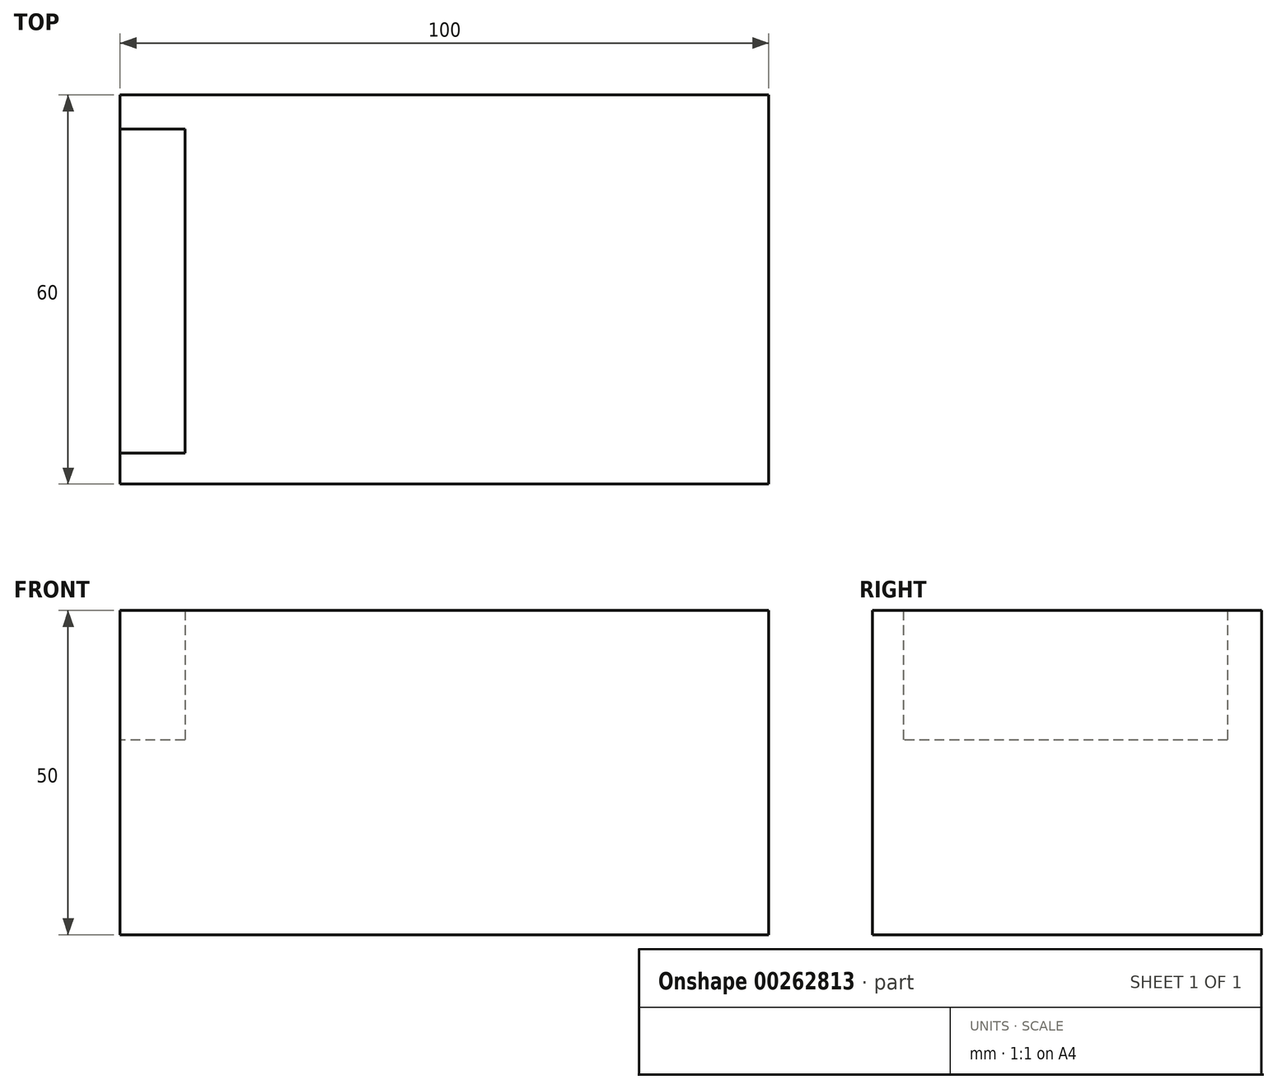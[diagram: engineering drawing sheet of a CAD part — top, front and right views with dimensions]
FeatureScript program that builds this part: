
annotation { "Feature Type Name" : "Feature", "Feature Type Description" : "" }
export const myFeature = defineFeature(function(context is Context, id is Id, definition is map)
    precondition{}
    {
        {
            var Q0;
            Q0=qCreatedBy(makeId("Front.planeOp"),FACE);
            var sketch = newSketch(context, id + "F0", { "sketchPlane" : qUnion([Q0])});
            skLineSegment(sketch, "E0.bottom", {"start": v(-50.72, 25.88) * mm, "end": v(49.28, 25.88) * mm});
            skLineSegment(sketch, "E0.top", {"start": v(-50.72, -24.12) * mm, "end": v(49.28, -24.12) * mm});
            skLineSegment(sketch, "E0.left", {"start": v(-50.72, 25.88) * mm, "end": v(-50.72, -24.12) * mm});
            skLineSegment(sketch, "E0.right", {"start": v(49.28, 25.88) * mm, "end": v(49.28, -24.12) * mm});
            skLineSegment(sketch, "E1.bottom", {"start": v(-50.72, -4.12) * mm, "end": v(-30.72, -4.12) * mm});
            skLineSegment(sketch, "E1.top", {"start": v(-50.72, -24.12) * mm, "end": v(-30.72, -24.12) * mm});
            skLineSegment(sketch, "E1.left", {"start": v(-50.72, -4.12) * mm, "end": v(-50.72, -24.12) * mm});
            skLineSegment(sketch, "E1.right", {"start": v(-30.72, -4.12) * mm, "end": v(-30.72, -24.12) * mm});
            skLineSegment(sketch, "E2.bottom", {"start": v(49.28, 5.88) * mm, "end": v(9.28, 5.88) * mm});
            skLineSegment(sketch, "E2.top", {"start": v(49.28, -24.12) * mm, "end": v(9.28, -24.12) * mm});
            skLineSegment(sketch, "E2.left", {"start": v(49.28, 5.88) * mm, "end": v(49.28, -24.12) * mm});
            skLineSegment(sketch, "E2.right", {"start": v(9.28, 5.88) * mm, "end": v(9.28, -24.12) * mm});
            skSolve(sketch);
        }
        {
            var Q0;
            Q0=makeQuery(id+"F0.imprint","IMPRINT",FACE,{"disambiguationData":[TD([[makeQuery(id+"F0.imprint","IMPRINT",EDGE,{"derivedFrom":sQuery(id+"F0.wireOp",EDGE,"E0.bottom")}),-1.0]])]});
            var Q1;
            Q1=makeQuery(id+"F0.imprint","IMPRINT",FACE,{"disambiguationData":[TD([[makeQuery(id+"F0.imprint","IMPRINT",EDGE,{"derivedFrom":sQuery(id+"F0.wireOp",EDGE,"E1.bottom")}),-1.0]])]});
            var Q2;
            Q2=makeQuery(id+"F0.imprint","IMPRINT",FACE,{"disambiguationData":[TD([[makeQuery(id+"F0.imprint","IMPRINT",EDGE,{"derivedFrom":sQuery(id+"F0.wireOp",EDGE,"E2.bottom")}),1.0]])]});
            extrude(context, id + "F1", {"entities" : qUnion([Q0, Q1, Q2]), "oppositeDirection" : true, "depth" : 60 * mm});
        }
        {
            var Q0;
            Q0=makeQuery(id+"F1.opExtrude","CAP_FACE",FACE,{"disambiguationData":[OSD([sQuery(id+"F0.wireOp",EDGE,"E0.bottom"),sQuery(id+"F0.wireOp",EDGE,"E0.top"),sQuery(id+"F0.wireOp",EDGE,"E0.left"),sQuery(id+"F0.wireOp",EDGE,"E0.right"),sQuery(id+"F0.wireOp",EDGE,"E1.top"),sQuery(id+"F0.wireOp",EDGE,"E1.left")])],"isStart":false});
            var sketch = newSketch(context, id + "F2", { "sketchPlane" : qUnion([Q0])});
            skLineSegment(sketch, "E3.bottom", {"start": v(30.72, -4.12) * mm, "end": v(50.72, -4.12) * mm});
            skLineSegment(sketch, "E3.top", {"start": v(30.72, -24.12) * mm, "end": v(50.72, -24.12) * mm});
            skLineSegment(sketch, "E3.left", {"start": v(30.72, -4.12) * mm, "end": v(30.72, -24.12) * mm});
            skLineSegment(sketch, "E3.right", {"start": v(50.72, -4.12) * mm, "end": v(50.72, -24.12) * mm});
            skLineSegment(sketch, "E4.bottom", {"start": v(-9.28, 5.88) * mm, "end": v(-49.28, 5.88) * mm});
            skLineSegment(sketch, "E4.top", {"start": v(-9.28, -24.12) * mm, "end": v(-49.28, -24.12) * mm});
            skLineSegment(sketch, "E4.left", {"start": v(-9.28, 5.88) * mm, "end": v(-9.28, -24.12) * mm});
            skLineSegment(sketch, "E4.right", {"start": v(-49.28, 5.88) * mm, "end": v(-49.28, -24.12) * mm});
            skSolve(sketch);
        }
        {
            var Q0;
            Q0=makeQuery(id+"F1.opExtrude","SWEPT_FACE",FACE,{"disambiguationData":[OSD([sQuery(id+"F0.wireOp",EDGE,"E0.left"),sQuery(id+"F0.wireOp",EDGE,"E1.left")])]});
            var sketch = newSketch(context, id + "F3", { "sketchPlane" : qUnion([Q0])});
            skLineSegment(sketch, "E5.bottom", {"start": v(-54.76, 25.88) * mm, "end": v(-4.76, 25.88) * mm});
            skLineSegment(sketch, "E5.top", {"start": v(-54.76, 5.88) * mm, "end": v(-4.76, 5.88) * mm});
            skLineSegment(sketch, "E5.left", {"start": v(-54.76, 25.88) * mm, "end": v(-54.76, 5.88) * mm});
            skLineSegment(sketch, "E5.right", {"start": v(-4.76, 25.88) * mm, "end": v(-4.76, 5.88) * mm});
            skSolve(sketch);
        }
        {
            var Q0;
            Q0 = qSketchRegion(id + "F3", true);
            extrude(context, id + "F4", {"entities" : qUnion([Q0]), "operationType" : NewBodyOperationType.REMOVE, "oppositeDirection" : true, "depth" : 10 * mm});
        }
    });
